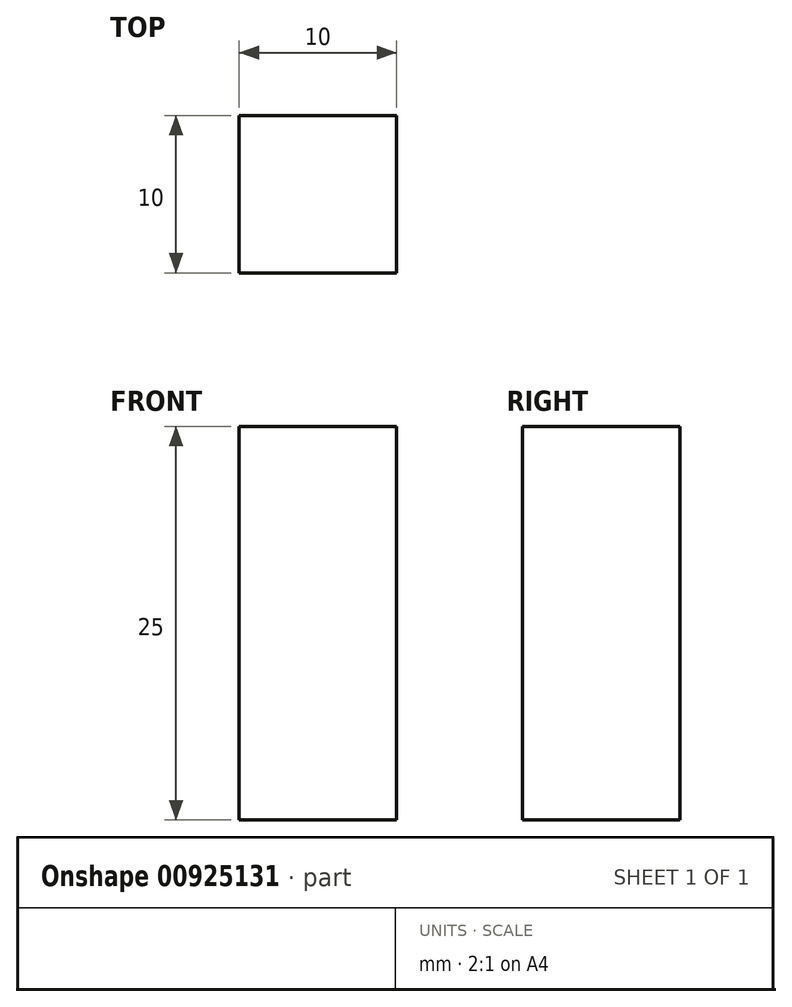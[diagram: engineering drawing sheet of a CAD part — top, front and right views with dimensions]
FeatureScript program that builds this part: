
annotation { "Feature Type Name" : "Feature", "Feature Type Description" : "" }
export const myFeature = defineFeature(function(context is Context, id is Id, definition is map)
    precondition{}
    {
        {
            var Q0;
            Q0=qCreatedBy(makeId("Top.planeOp"),FACE);
            var sketch = newSketch(context, id + "F0", { "sketchPlane" : qUnion([Q0])});
            skLineSegment(sketch, "E0.bottom", {"start": v(0, 0) * mm, "end": v(-10, 0) * mm});
            skLineSegment(sketch, "E0.top", {"start": v(0, 10) * mm, "end": v(-10, 10) * mm});
            skLineSegment(sketch, "E0.left", {"start": v(0, 0) * mm, "end": v(0, 10) * mm});
            skLineSegment(sketch, "E0.right", {"start": v(-10, 0) * mm, "end": v(-10, 10) * mm});
            skSolve(sketch);
        }
        {
            var Q0;
            Q0 = qSketchRegion(id + "F0", true);
            extrude(context, id + "F1", {"entities" : qUnion([Q0]), "depth" : 25 * mm, "offsetDistance" : 25 * mm});
        }
    });
